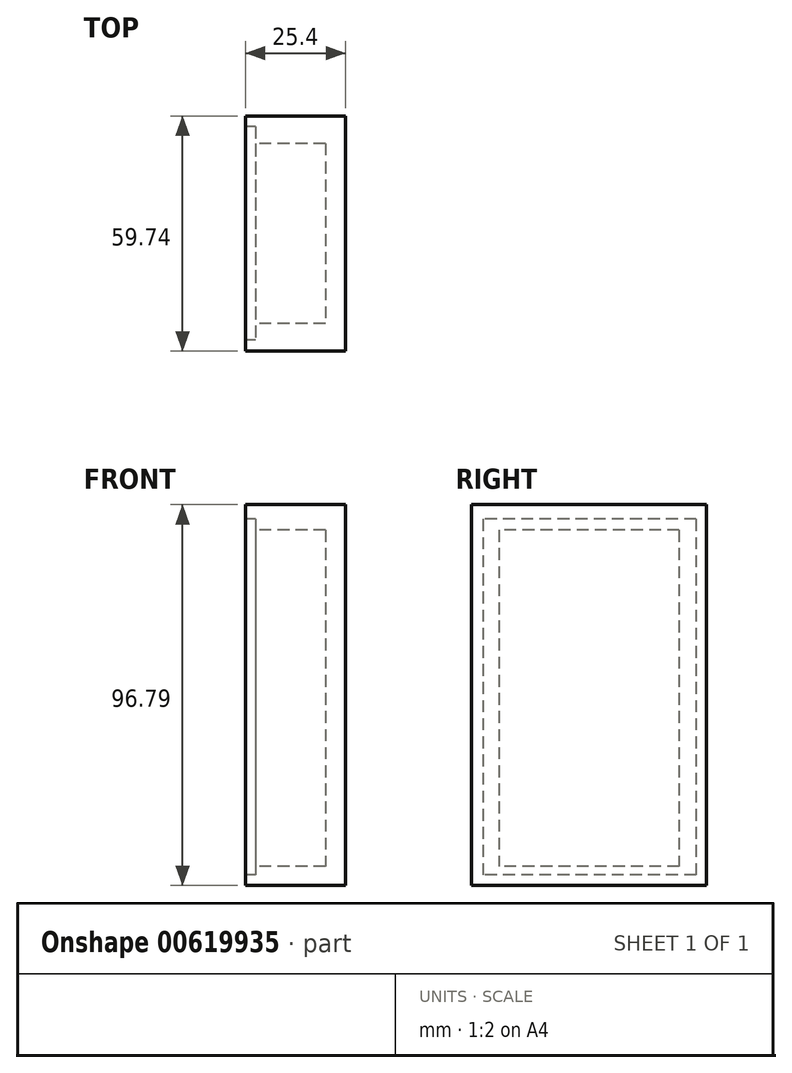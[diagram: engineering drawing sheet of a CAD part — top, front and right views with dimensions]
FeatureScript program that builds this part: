
annotation { "Feature Type Name" : "Feature", "Feature Type Description" : "" }
export const myFeature = defineFeature(function(context is Context, id is Id, definition is map)
    precondition{}
    {
        {
            var Q0;
            Q0=qCreatedBy(makeId("Right.planeOp"),FACE);
            var sketch = newSketch(context, id + "F0", { "sketchPlane" : qUnion([Q0])});
            skLineSegment(sketch, "E0.bottom", {"start": v(-35.22, 48.75) * mm, "end": v(24.52, 48.75) * mm});
            skLineSegment(sketch, "E0.top", {"start": v(-35.22, -48.04) * mm, "end": v(24.52, -48.04) * mm});
            skLineSegment(sketch, "E0.left", {"start": v(-35.22, 48.75) * mm, "end": v(-35.22, -48.04) * mm});
            skLineSegment(sketch, "E0.right", {"start": v(24.52, 48.75) * mm, "end": v(24.52, -48.04) * mm});
            skSolve(sketch);
        }
        {
            var Q0;
            Q0=makeQuery(id+"F0.imprint","IMPRINT",FACE,{"disambiguationData":[TD([[makeQuery(id+"F0.imprint","IMPRINT",EDGE,{"derivedFrom":sQuery(id+"F0.wireOp",EDGE,"E0.bottom")}),-1.0]])]});
            extrude(context, id + "F1", {"entities" : qUnion([Q0]), "depth" : 25.4 * mm, "offsetDistance" : 25.4 * mm});
        }
        {
            var Q0;
            Q0=makeQuery(id+"F1.opExtrude","CAP_FACE",FACE,{"disambiguationData":[OSD([sQuery(id+"F0.wireOp",EDGE,"E0.bottom"),sQuery(id+"F0.wireOp",EDGE,"E0.top"),sQuery(id+"F0.wireOp",EDGE,"E0.left"),sQuery(id+"F0.wireOp",EDGE,"E0.right")])],"isStart":true});
            var sketch = newSketch(context, id + "F2", { "sketchPlane" : qUnion([Q0])});
            skLineSegment(sketch, "E1.bottom", {"start": v(-17.52, 42.28) * mm, "end": v(28.24, 42.28) * mm});
            skLineSegment(sketch, "E1.top", {"start": v(-17.52, -43.17) * mm, "end": v(28.24, -43.17) * mm});
            skLineSegment(sketch, "E1.left", {"start": v(-17.52, 42.28) * mm, "end": v(-17.52, -43.17) * mm});
            skLineSegment(sketch, "E1.right", {"start": v(28.24, 42.28) * mm, "end": v(28.24, -43.17) * mm});
            skSolve(sketch);
        }
        {
            var Q0;
            Q0=makeQuery(id+"F2.imprint","IMPRINT",FACE,{"disambiguationData":[TD([[makeQuery(id+"F2.imprint","IMPRINT",EDGE,{"derivedFrom":sQuery(id+"F2.wireOp",EDGE,"E1.bottom")}),-1.0]])]});
            extrude(context, id + "F3", {"entities" : qUnion([Q0]), "operationType" : NewBodyOperationType.REMOVE, "oppositeDirection" : true, "depth" : 20.32 * mm, "offsetDistance" : 25.4 * mm});
        }
        {
            var Q0;
            Q0=makeQuery(id+"F1.opExtrude","CAP_FACE",FACE,{"disambiguationData":[OSD([sQuery(id+"F0.wireOp",EDGE,"E0.bottom"),sQuery(id+"F0.wireOp",EDGE,"E0.top"),sQuery(id+"F0.wireOp",EDGE,"E0.left"),sQuery(id+"F0.wireOp",EDGE,"E0.right")])],"isStart":true});
            var sketch = newSketch(context, id + "F4", { "sketchPlane" : qUnion([Q0])});
            skLineSegment(sketch, "E2.bottom", {"start": v(-21.83, 45.04) * mm, "end": v(32.37, 45.04) * mm});
            skLineSegment(sketch, "E2.top", {"start": v(-21.83, -45.33) * mm, "end": v(32.37, -45.33) * mm});
            skLineSegment(sketch, "E2.left", {"start": v(-21.83, 45.04) * mm, "end": v(-21.83, -45.33) * mm});
            skLineSegment(sketch, "E2.right", {"start": v(32.37, 45.04) * mm, "end": v(32.37, -45.33) * mm});
            skSolve(sketch);
        }
        {
            var Q0;
            Q0=makeQuery(id+"F4.imprint","IMPRINT",FACE,{"disambiguationData":[TD([[makeQuery(id+"F4.imprint","IMPRINT",EDGE,{"derivedFrom":sQuery(id+"F4.wireOp",EDGE,"E2.bottom")}),-1.0]])]});
            extrude(context, id + "F5", {"entities" : qUnion([Q0]), "operationType" : NewBodyOperationType.REMOVE, "oppositeDirection" : true, "depth" : 2.54 * mm, "offsetDistance" : 25.4 * mm});
        }
    });
